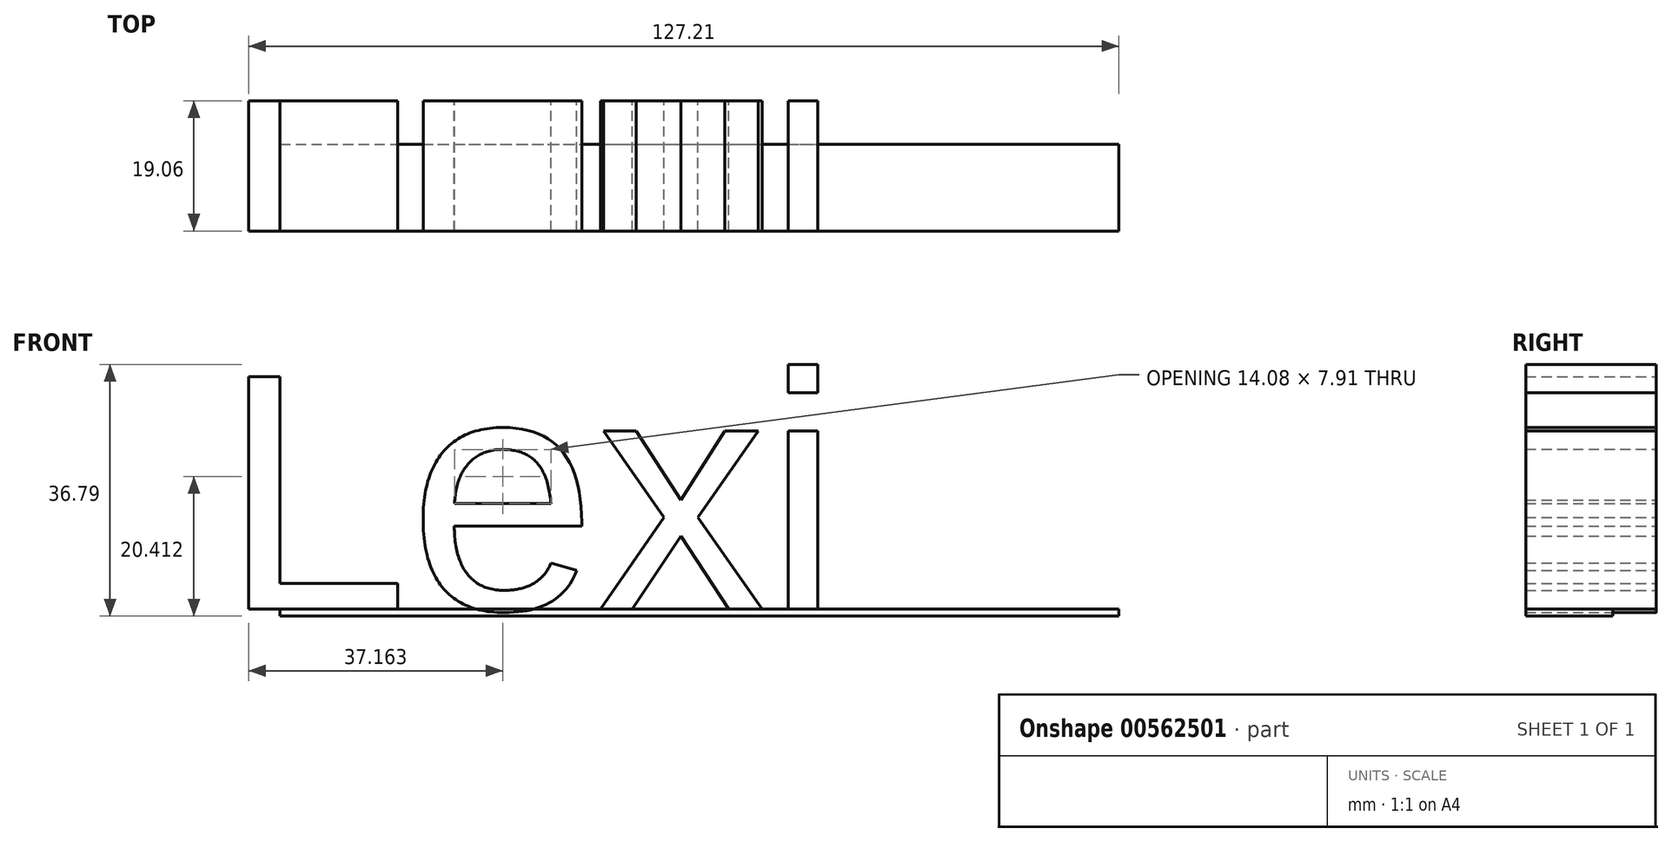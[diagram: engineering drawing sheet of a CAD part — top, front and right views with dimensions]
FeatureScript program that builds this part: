
annotation { "Feature Type Name" : "Feature", "Feature Type Description" : "" }
export const myFeature = defineFeature(function(context is Context, id is Id, definition is map)
    precondition{}
    {
        {
            var Q0;
            Q0=qCreatedBy(makeId("Front.planeOp"),FACE);
            var sketch = newSketch(context, id + "F0", { "sketchPlane" : qUnion([Q0])});
            skText(sketch, "E0", { "text": "Lexi", "fontName": "Arimo-Regular.ttf"});
            skPoint(sketch, "E1", {"position": v(0, 17.78) * mm});
            const initialGuessF0  = {"E0": [-0.04535, 0, 1, 0, 0.03556]};
            skSetInitialGuess(sketch, initialGuessF0);
            skSolve(sketch);
        }
        {
            var Q0;
            Q0=qSketchRegion(id+"F0",true);
            extrude(context, id + "F1", {"entities" : qUnion([Q0]), "endBound" : BoundingType.SYMMETRIC, "depth" : 19.05 * mm, "offsetDistance" : 25.4 * mm});
        }
        {
            var Q0;
            Q0=qCreatedBy(makeId("Top.planeOp"),FACE);
            var sketch = newSketch(context, id + "F2", { "sketchPlane" : qUnion([Q0])});
            skLineSegment(sketch, "E2.bottom", {"start": v(-36.7, 3.18) * mm, "end": v(85.91, 3.18) * mm});
            skLineSegment(sketch, "E2.top", {"start": v(-36.7, -9.53) * mm, "end": v(85.91, -9.53) * mm});
            skLineSegment(sketch, "E2.left", {"start": v(-36.7, 3.18) * mm, "end": v(-36.7, -9.53) * mm});
            skLineSegment(sketch, "E2.right", {"start": v(85.91, 3.18) * mm, "end": v(85.91, -9.53) * mm});
            skSolve(sketch);
        }
        {
            var Q0;
            Q0=makeQuery(id+"F2.imprint","IMPRINT",FACE,{"disambiguationData":[TD([[makeQuery(id+"F2.imprint","IMPRINT",EDGE,{"derivedFrom":sQuery(id+"F2.wireOp",EDGE,"dJWAcAFj-qDJE-pdfo-wJ6e-4VfiU2RZUm0C.bottom")}),1.0]])]});
            var Q1;
            Q1=makeQuery(id+"F2.imprint","IMPRINT",FACE,{"disambiguationData":[TD([[makeQuery(id+"F2.imprint","IMPRINT",EDGE,{"derivedFrom":sQuery(id+"F2.wireOp",EDGE,"E2.bottom")}),-1.0]])]});
            extrude(context, id + "F3", {"entities" : qUnion([Q0, Q1]), "oppositeDirection" : true, "depth" : 1 * mm, "offsetDistance" : 25.4 * mm});
        }
    });
